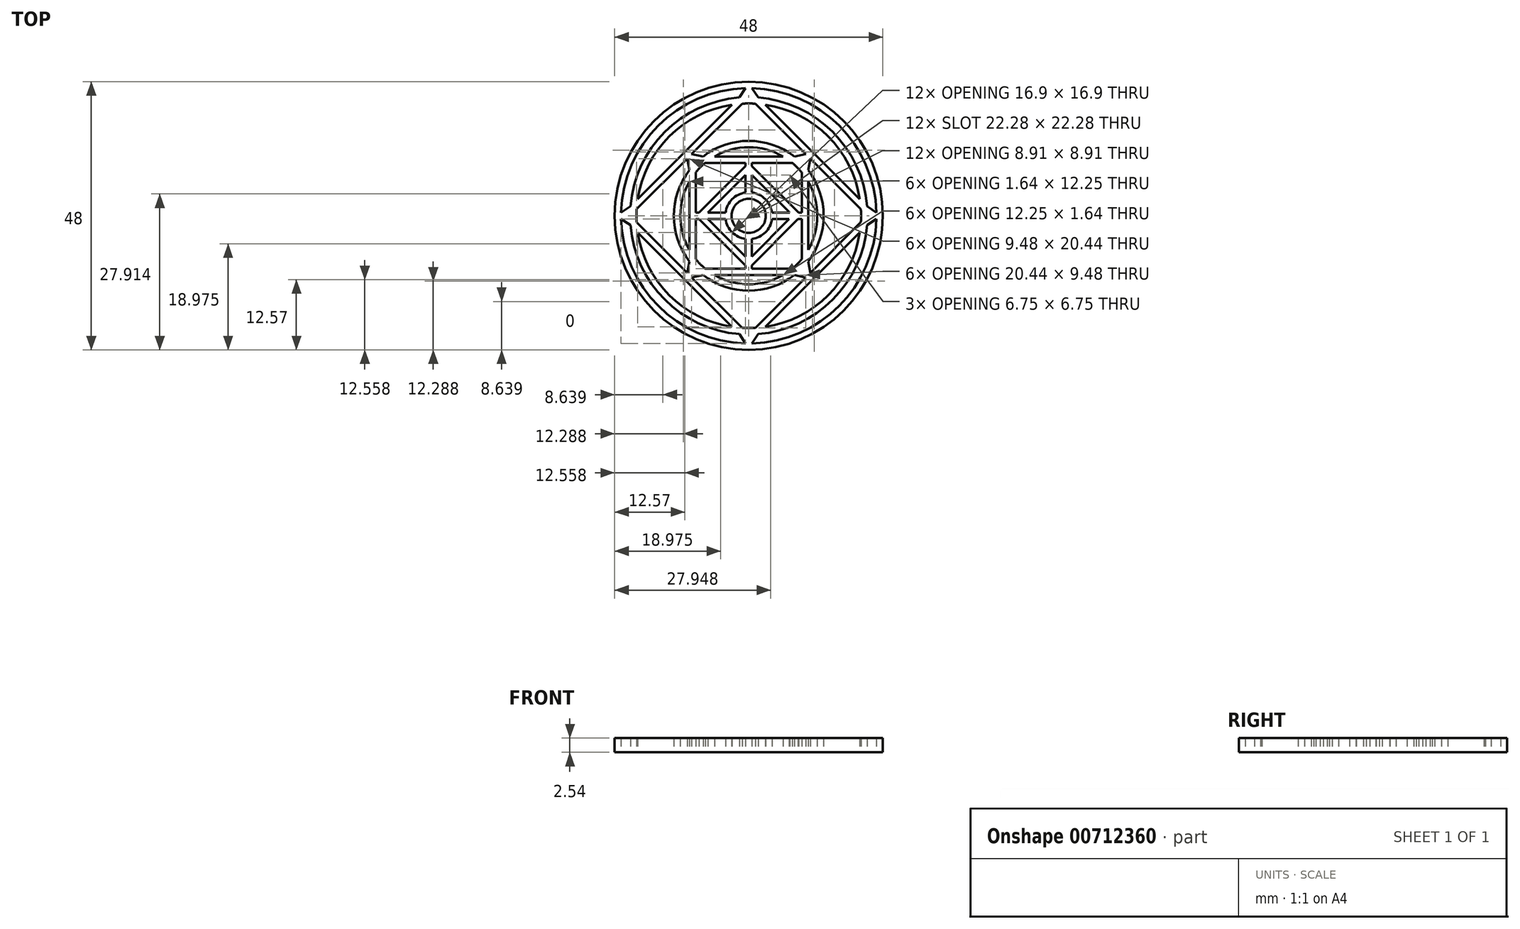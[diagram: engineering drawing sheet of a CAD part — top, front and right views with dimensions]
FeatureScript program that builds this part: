
annotation { "Feature Type Name" : "Feature", "Feature Type Description" : "" }
export const myFeature = defineFeature(function(context is Context, id is Id, definition is map)
    precondition{}
    {
        {
            var Q0;
            Q0=qCreatedBy(makeId("Top.planeOp"),FACE);
            var sketch = newSketch(context, id + "F0", { "sketchPlane" : qUnion([Q0])});
            skArc(sketch, "E0.0", {"start": v(0.57, -22.85) * mm, "mid": v(16.16, -16.16) * mm, "end": v(22.85, -0.57) * mm});
            skLineSegment(sketch, "E1.0", {"start": v(1.18, 20.07) * mm, "end": v(10.22, 11.03) * mm});
            skLineSegment(sketch, "E2.0", {"start": v(-20.07, 1.18) * mm, "end": v(-11.03, 10.22) * mm});
            skLineSegment(sketch, "E3.0", {"start": v(-1.18, -20.07) * mm, "end": v(-10.22, -11.03) * mm});
            skLineSegment(sketch, "E4.0", {"start": v(20.07, -1.18) * mm, "end": v(11.03, -10.22) * mm});
            skLineSegment(sketch, "E5.0", {"start": v(-7.78, 9.48) * mm, "end": v(-0.57, 9.48) * mm});
            skLineSegment(sketch, "E6.0", {"start": v(-9.48, 7.78) * mm, "end": v(-9.48, 0.57) * mm});
            skLineSegment(sketch, "E7.0", {"start": v(-7.78, -9.48) * mm, "end": v(-0.57, -9.48) * mm});
            skLineSegment(sketch, "E8.0", {"start": v(9.48, 7.78) * mm, "end": v(9.48, 0.57) * mm});
            skLineSegment(sketch, "E9", {"start": v(-0.57, 8.9) * mm, "end": v(-1.83, 7.65) * mm});
            skLineSegment(sketch, "E10", {"start": v(-8.9, -0.57) * mm, "end": v(-7.65, -1.83) * mm});
            skLineSegment(sketch, "E11", {"start": v(0.57, -8.9) * mm, "end": v(8.83, -0.57) * mm});
            skLineSegment(sketch, "E12", {"start": v(8.9, 0.57) * mm, "end": v(7.65, 1.83) * mm});
            skLineSegment(sketch, "E13.0", {"start": v(7.33, 0.54) * mm, "end": v(0.57, 7.3) * mm});
            skLineSegment(sketch, "E14.0", {"start": v(-7.3, -0.57) * mm, "end": v(-0.57, -7.3) * mm});
            skLineSegment(sketch, "E15.0", {"start": v(-0.57, 7.3) * mm, "end": v(-7.3, 0.57) * mm});
            skLineSegment(sketch, "E16.0", {"start": v(-0.81, -8.67) * mm, "end": v(-0.8, -8.67) * mm});
            skLineSegment(sketch, "E17.trimOffspring", {"start": v(0.57, -7.28) * mm, "end": v(7.22, -0.57) * mm});
            skLineSegment(sketch, "E18.trimOffspring", {"start": v(0.8, -8.67) * mm, "end": v(0.8, -8.67) * mm});
            skPoint(sketch, "E19.orphan", {"position": v(0, 9.48) * mm});
            skLineSegment(sketch, "E20.trimOffspring", {"start": v(0.57, 9.48) * mm, "end": v(7.78, 9.48) * mm});
            skLineSegment(sketch, "E21.trimOffspring", {"start": v(0.57, 9.48) * mm, "end": v(0.57, 8.9) * mm});
            skLineSegment(sketch, "E22.trimOffspring", {"start": v(-0.57, 9.48) * mm, "end": v(-0.57, 8.9) * mm});
            skLineSegment(sketch, "E23.trimOffspring", {"start": v(-0.57, -8.9) * mm, "end": v(-0.57, -9.48) * mm});
            skLineSegment(sketch, "E24.trimOffspring", {"start": v(0.57, -8.9) * mm, "end": v(0.57, -9.48) * mm});
            skPoint(sketch, "E25.orphan", {"position": v(0, -9.48) * mm});
            skLineSegment(sketch, "E26.trimOffspring", {"start": v(0.57, -9.48) * mm, "end": v(7.78, -9.48) * mm});
            skArc(sketch, "E27.trimOffspring", {"start": v(22.85, 0.57) * mm, "mid": v(16.16, 16.16) * mm, "end": v(0.57, 22.85) * mm});
            skArc(sketch, "E28.trimOffspring", {"start": v(-22.85, -0.57) * mm, "mid": v(-16.16, -16.16) * mm, "end": v(-0.57, -22.85) * mm});
            skPoint(sketch, "E29.orphan", {"position": v(-9.48, 0) * mm});
            skLineSegment(sketch, "E30.trimOffspring", {"start": v(-9.48, 0.57) * mm, "end": v(-8.9, 0.57) * mm});
            skLineSegment(sketch, "E31.trimOffspring", {"start": v(-9.48, -0.57) * mm, "end": v(-8.9, -0.57) * mm});
            skLineSegment(sketch, "E32.trimOffspring", {"start": v(-9.48, -0.57) * mm, "end": v(-9.48, -7.78) * mm});
            skLineSegment(sketch, "E33.trimOffspring", {"start": v(9.48, -0.57) * mm, "end": v(9.48, -7.78) * mm});
            skLineSegment(sketch, "E34.trimOffspring", {"start": v(8.9, 0.57) * mm, "end": v(9.48, 0.57) * mm});
            skLineSegment(sketch, "E35.trimOffspring", {"start": v(8.83, -0.57) * mm, "end": v(9.48, -0.57) * mm});
            skArc(sketch, "E36", {"start": v(1.68, -21.18) * mm, "mid": v(15.02, -15.02) * mm, "end": v(21.18, -1.68) * mm});
            skArc(sketch, "E37.0", {"start": v(-1.18, -20.07) * mm, "mid": v(0, -20.1) * mm, "end": v(1.18, -20.07) * mm});
            skPoint(sketch, "E38.orphan", {"position": v(0, -21.24) * mm});
            skArc(sketch, "E39.trimOffspring", {"start": v(2.98, -19.88) * mm, "mid": v(14.21, -14.21) * mm, "end": v(19.88, -2.98) * mm});
            skLineSegment(sketch, "E40.trimOffspring", {"start": v(-2.98, -19.88) * mm, "end": v(-19.88, -2.98) * mm});
            skArc(sketch, "E41.trimOffspring", {"start": v(-20.07, 1.18) * mm, "mid": v(-20.1, 0) * mm, "end": v(-20.07, -1.18) * mm});
            skArc(sketch, "E42.trimOffspring", {"start": v(-19.88, -2.98) * mm, "mid": v(-14.21, -14.21) * mm, "end": v(-2.98, -19.88) * mm});
            skPoint(sketch, "E43.orphan", {"position": v(-21.24, 0) * mm});
            skArc(sketch, "E44.trimOffspring", {"start": v(-21.18, -1.68) * mm, "mid": v(-15.02, -15.02) * mm, "end": v(-1.68, -21.18) * mm});
            skLineSegment(sketch, "E45.trimOffspring", {"start": v(-19.88, 2.98) * mm, "end": v(-2.98, 19.88) * mm});
            skLineSegment(sketch, "E46", {"start": v(-21.18, 1.68) * mm, "end": v(-22.85, 0.57) * mm});
            skLineSegment(sketch, "E47", {"start": v(-21.18, -1.68) * mm, "end": v(-22.85, -0.57) * mm});
            skPoint(sketch, "E48.orphan", {"position": v(0, 21.24) * mm});
            skLineSegment(sketch, "E49.trimOffspring", {"start": v(2.98, 19.88) * mm, "end": v(19.88, 2.98) * mm});
            skArc(sketch, "E50.trimOffspring", {"start": v(-2.98, 19.88) * mm, "mid": v(-14.21, 14.21) * mm, "end": v(-19.88, 2.98) * mm});
            skArc(sketch, "E51.trimOffspring", {"start": v(1.18, 20.07) * mm, "mid": v(0, 20.1) * mm, "end": v(-1.18, 20.07) * mm});
            skArc(sketch, "E52.trimOffspring", {"start": v(-1.68, 21.18) * mm, "mid": v(-15.02, 15.02) * mm, "end": v(-21.18, 1.68) * mm});
            skLineSegment(sketch, "E53", {"start": v(-0.57, 22.85) * mm, "end": v(-1.68, 21.18) * mm});
            skLineSegment(sketch, "E54", {"start": v(0.57, 22.85) * mm, "end": v(1.68, 21.18) * mm});
            skLineSegment(sketch, "E55", {"start": v(-1.68, -21.18) * mm, "end": v(-0.57, -22.85) * mm});
            skLineSegment(sketch, "E56", {"start": v(1.68, -21.18) * mm, "end": v(0.57, -22.85) * mm});
            skPoint(sketch, "E57.orphan", {"position": v(21.24, 0) * mm});
            skLineSegment(sketch, "E58.trimOffspring", {"start": v(19.88, -2.98) * mm, "end": v(2.98, -19.88) * mm});
            skArc(sketch, "E59.trimOffspring", {"start": v(20.07, -1.18) * mm, "mid": v(20.1, 0) * mm, "end": v(20.07, 1.18) * mm});
            skArc(sketch, "E60.trimOffspring", {"start": v(19.88, 2.98) * mm, "mid": v(14.21, 14.21) * mm, "end": v(2.98, 19.88) * mm});
            skArc(sketch, "E61.trimOffspring", {"start": v(21.18, 1.68) * mm, "mid": v(15.02, 15.02) * mm, "end": v(1.68, 21.18) * mm});
            skLineSegment(sketch, "E62", {"start": v(21.18, 1.68) * mm, "end": v(22.85, 0.57) * mm});
            skLineSegment(sketch, "E63", {"start": v(21.18, -1.68) * mm, "end": v(22.85, -0.57) * mm});
            skLineSegment(sketch, "E64.trimOffspring", {"start": v(-11.03, -10.22) * mm, "end": v(-20.07, -1.18) * mm});
            skLineSegment(sketch, "E65.trimOffspring", {"start": v(11.03, 10.22) * mm, "end": v(20.07, 1.18) * mm});
            skPoint(sketch, "E66.orphan", {"position": v(10.62, -10.62) * mm});
            skLineSegment(sketch, "E67.trimOffspring", {"start": v(10.22, -11.03) * mm, "end": v(1.18, -20.07) * mm});
            skLineSegment(sketch, "E68.trimOffspring", {"start": v(-10.22, 11.03) * mm, "end": v(-1.18, 20.07) * mm});
            skArc(sketch, "E69", {"start": v(-10.62, 8.18) * mm, "mid": v(-13.4, 0) * mm, "end": v(-10.62, -8.18) * mm});
            skArc(sketch, "E70.0", {"start": v(-7.78, 9.48) * mm, "mid": v(-8.67, 8.67) * mm, "end": v(-9.48, 7.78) * mm});
            skLineSegment(sketch, "E71.trimOffspring", {"start": v(-6.13, 10.62) * mm, "end": v(6.13, 10.62) * mm});
            skPoint(sketch, "E72.orphan", {"position": v(-9.48, 9.48) * mm});
            skLineSegment(sketch, "E73.trimOffspring", {"start": v(-10.62, 6.13) * mm, "end": v(-10.62, -6.13) * mm});
            skArc(sketch, "E74.trimOffspring", {"start": v(-10.62, 6.13) * mm, "mid": v(-12.26, 0) * mm, "end": v(-10.62, -6.13) * mm});
            skPoint(sketch, "E75.orphan", {"position": v(9.48, -9.48) * mm});
            skArc(sketch, "E76.trimOffspring", {"start": v(10.62, -8.18) * mm, "mid": v(13.4, 0) * mm, "end": v(10.62, 8.18) * mm});
            skArc(sketch, "E77.trimOffspring", {"start": v(10.62, -6.13) * mm, "mid": v(12.26, 0) * mm, "end": v(10.62, 6.13) * mm});
            skArc(sketch, "E78.trimOffspring", {"start": v(7.78, -9.48) * mm, "mid": v(8.67, -8.67) * mm, "end": v(9.48, -7.78) * mm});
            skPoint(sketch, "E79.orphan", {"position": v(-9.48, -9.48) * mm});
            skLineSegment(sketch, "E80.trimOffspring", {"start": v(-6.13, -10.62) * mm, "end": v(6.13, -10.62) * mm});
            skArc(sketch, "E81.trimOffspring", {"start": v(-8.18, -10.62) * mm, "mid": v(0, -13.4) * mm, "end": v(8.18, -10.62) * mm});
            skArc(sketch, "E82.trimOffspring", {"start": v(-9.48, -7.78) * mm, "mid": v(-8.67, -8.67) * mm, "end": v(-7.78, -9.48) * mm});
            skArc(sketch, "E83.trimOffspring", {"start": v(-6.13, -10.62) * mm, "mid": v(0, -12.26) * mm, "end": v(6.13, -10.62) * mm});
            skPoint(sketch, "E84.orphan", {"position": v(9.48, 9.48) * mm});
            skLineSegment(sketch, "E85.trimOffspring", {"start": v(10.62, 6.13) * mm, "end": v(10.62, -6.13) * mm});
            skArc(sketch, "E86.trimOffspring", {"start": v(8.18, 10.62) * mm, "mid": v(0, 13.4) * mm, "end": v(-8.18, 10.62) * mm});
            skArc(sketch, "E87.trimOffspring", {"start": v(9.48, 7.78) * mm, "mid": v(8.67, 8.67) * mm, "end": v(7.78, 9.48) * mm});
            skArc(sketch, "E88.trimOffspring", {"start": v(6.13, 10.62) * mm, "mid": v(0, 12.26) * mm, "end": v(-6.13, 10.62) * mm});
            skLineSegment(sketch, "E89", {"start": v(8.18, 10.62) * mm, "end": v(10.22, 11.03) * mm});
            skLineSegment(sketch, "E90", {"start": v(11.03, 10.22) * mm, "end": v(10.62, 8.18) * mm});
            skLineSegment(sketch, "E91", {"start": v(-10.62, -8.18) * mm, "end": v(-11.03, -10.22) * mm});
            skLineSegment(sketch, "E92", {"start": v(-8.18, -10.62) * mm, "end": v(-10.22, -11.03) * mm});
            skLineSegment(sketch, "E93", {"start": v(-10.62, 8.18) * mm, "end": v(-11.03, 10.22) * mm});
            skLineSegment(sketch, "E94", {"start": v(-10.22, 11.03) * mm, "end": v(-8.18, 10.62) * mm});
            skLineSegment(sketch, "E95", {"start": v(8.18, -10.62) * mm, "end": v(10.22, -11.03) * mm});
            skLineSegment(sketch, "E96", {"start": v(11.03, -10.22) * mm, "end": v(10.62, -8.18) * mm});
            skLineSegment(sketch, "E97.trimOffspring", {"start": v(-7.65, 1.83) * mm, "end": v(-8.9, 0.57) * mm});
            skLineSegment(sketch, "E98.trimOffspring", {"start": v(1.83, 7.65) * mm, "end": v(0.57, 8.9) * mm});
            skLineSegment(sketch, "E99.trimOffspring", {"start": v(-1.83, -7.65) * mm, "end": v(-0.57, -8.9) * mm});
            skLineSegment(sketch, "E100", {"start": v(1.83, 7.65) * mm, "end": v(7.65, 1.83) * mm});
            skLineSegment(sketch, "E101", {"start": v(-7.65, -1.83) * mm, "end": v(-1.83, -7.65) * mm});
            skArc(sketch, "E102", {"start": v(0.57, -4.16) * mm, "mid": v(2.97, -2.97) * mm, "end": v(4.16, -0.57) * mm});
            skLineSegment(sketch, "E103", {"start": v(-7.65, 1.83) * mm, "end": v(-1.83, 7.65) * mm});
            skLineSegment(sketch, "E104", {"start": v(-7.3, 0.57) * mm, "end": v(-4.16, 0.56) * mm});
            skLineSegment(sketch, "E105", {"start": v(7.22, -0.57) * mm, "end": v(4.16, -0.57) * mm});
            skLineSegment(sketch, "E106", {"start": v(-0.57, 7.3) * mm, "end": v(-0.57, 4.16) * mm});
            skLineSegment(sketch, "E107", {"start": v(0.57, 7.3) * mm, "end": v(0.57, 4.16) * mm});
            skCircle(sketch, "E108", {"center": v(0, 0) * mm, "radius": 3.05 * mm});
            skLineSegment(sketch, "E109.trimOffspring", {"start": v(-4.16, -0.57) * mm, "end": v(-7.3, -0.57) * mm});
            skLineSegment(sketch, "E110.trimOffspring", {"start": v(4.16, 0.54) * mm, "end": v(7.33, 0.54) * mm});
            skLineSegment(sketch, "E111.trimOffspring", {"start": v(0.57, -4.16) * mm, "end": v(0.57, -7.28) * mm});
            skLineSegment(sketch, "E112.trimOffspring", {"start": v(-0.57, -4.16) * mm, "end": v(-0.57, -7.3) * mm});
            skArc(sketch, "E113.trimOffspring", {"start": v(-4.16, -0.57) * mm, "mid": v(-2.97, -2.97) * mm, "end": v(-0.57, -4.16) * mm});
            skArc(sketch, "E114.trimOffspring", {"start": v(-0.57, 4.16) * mm, "mid": v(-2.97, 2.96) * mm, "end": v(-4.16, 0.56) * mm});
            skArc(sketch, "E115.trimOffspring", {"start": v(4.16, 0.54) * mm, "mid": v(2.98, 2.96) * mm, "end": v(0.57, 4.16) * mm});
            skArc(sketch, "E116.trimOffspring", {"start": v(-0.57, 22.85) * mm, "mid": v(-16.16, 16.16) * mm, "end": v(-22.85, 0.57) * mm});
            skCircle(sketch, "E117.converted", {"center": v(0, 0) * mm, "radius": 24 * mm});
            skSolve(sketch);
        }
        {
            var Q0;
            Q0=makeQuery(id+"F0.imprint","IMPRINT",FACE,{"disambiguationData":[TD([[makeQuery(id+"F0.imprint","IMPRINT",EDGE,{"derivedFrom":sQuery(id+"F0.wireOp",EDGE,"E0.0")}),-1.0]])]});
            extrude(context, id + "F1", {"entities" : qUnion([Q0]), "depth" : 2.54 * mm, "offsetDistance" : 25.4 * mm});
        }
    });
